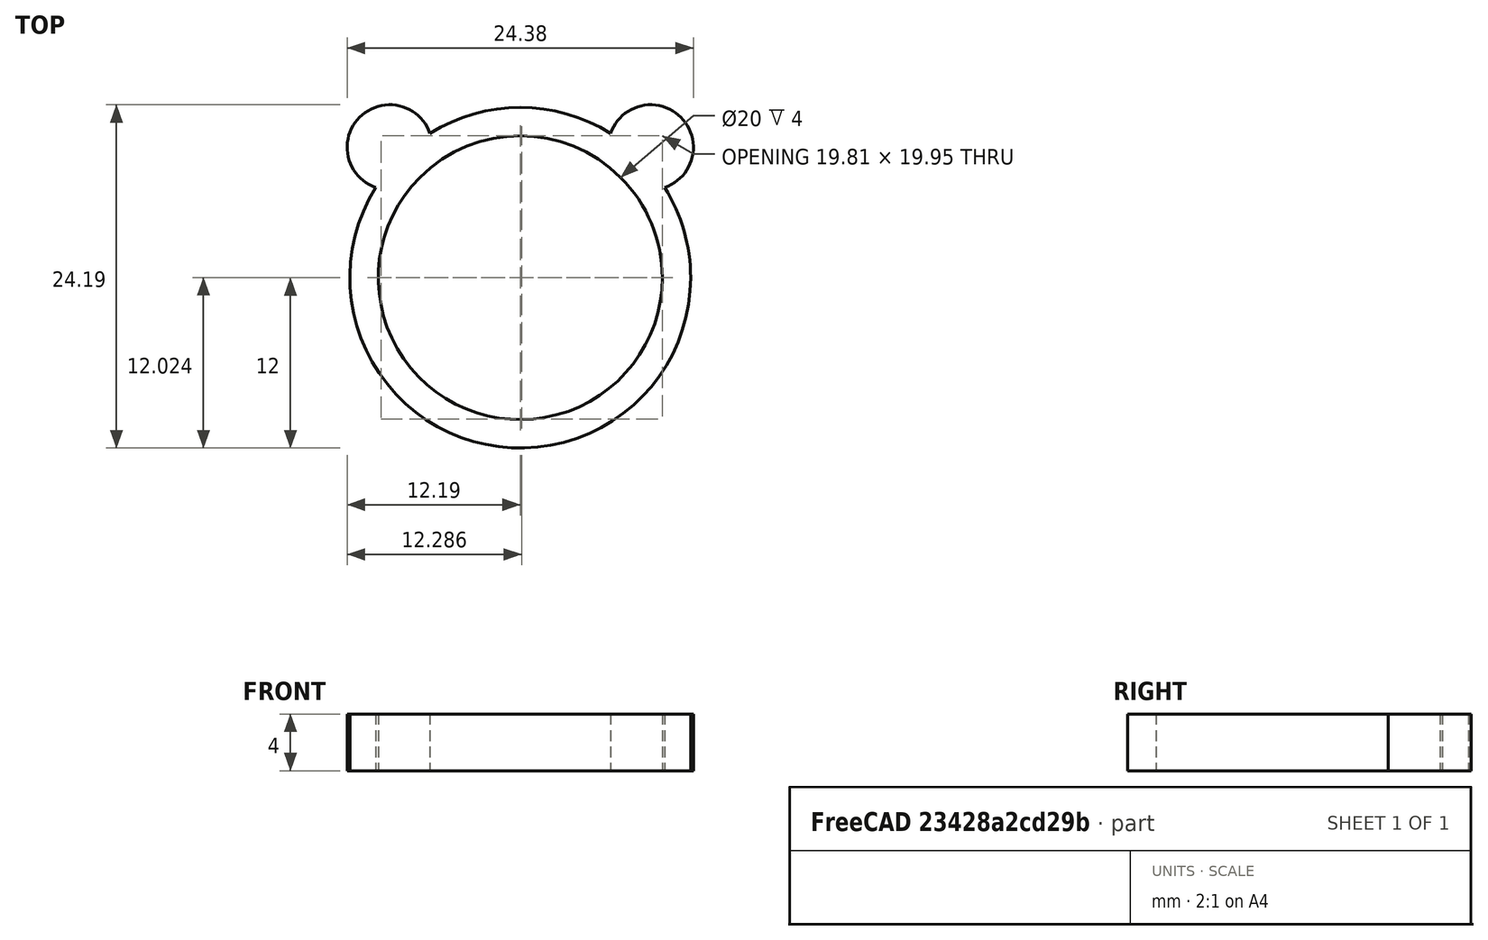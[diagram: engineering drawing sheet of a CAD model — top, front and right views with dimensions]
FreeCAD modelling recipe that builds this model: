
FCSTD DOCUMENT  (FreeCAD 0.17R12412 (Git))
Label: 04-ring-parametric
License: All rights reserved
LicenseURL: http://en.wikipedia.org/wiki/All_rights_reserved
objects: TechDraw::DrawViewDimension×4, Sketcher::SketchObject×2, PartDesign::Pad×2, TechDraw::DrawProjGroupItem×2, TechDraw::DrawHatch×2, PartDesign::Mirrored×1, PartDesign::Body×1, Spreadsheet::Sheet×1, TechDraw::DrawSVGTemplate×1, TechDraw::DrawProjGroup×1, TechDraw::DrawPage×1
note: 8 computed .brp shape members not serialized (recipe doc carries the construction recipe); baked Part::Feature solids carry a one-line shape summary decoded from their .brp

FEATURE [Sketcher::SketchObject] Sketch
  MapMode = 5
  Support = -> [XY_Plane]
  expr: Constraints[1] = param.R + 2
  expr: Constraints[3] = param.R
  sketch-geometry (2):
    g0: Circle CenterX=0 CenterY=0 CenterZ=0 NormalX=0 NormalY=0 NormalZ=1 AngleXU=0 Radius=12
    g1: Circle CenterX=0 CenterY=0 CenterZ=0 NormalX=0 NormalY=0 NormalZ=1 AngleXU=0 Radius=10
  constraints (4):
    c: Coincident(g0,g-1)
    c: Radius(g0) = 12
    c: Coincident(g1,g-1)
    c: Radius(g1) = 10
FEATURE [PartDesign::Pad] Pad
  Length = 4
  Length2 = 100
  Profile = -> Sketch
  Type = 0
  expr: Length = param.H
FEATURE [Sketcher::SketchObject] Sketch001
  ExternalGeometry = -> [Pad]
  MapMode = 5
  Support = -> [XY_Plane]
  expr: Constraints[4] = param.R + 3
  sketch-geometry (2):
    g0: Circle CenterX=-9.19239 CenterY=9.19239 CenterZ=0 NormalX=0 NormalY=0 NormalZ=1 AngleXU=0 Radius=3
    g1: LineSegment [constr] StartX=-9.19239 StartY=9.19239 StartZ=0 EndX=0 EndY=0 EndZ=0
  constraints (5):
    c: Radius(g0) = 3
    c: Coincident(g1,g0)
    c: Coincident(g1,g-1)
    c: Angle(g-2,g1) = 0.785398
    c: Distance(g1) = 13
FEATURE [PartDesign::Pad] Pad001
  BaseFeature = -> Pad
  Length = 3
  Length2 = 100
  Profile = -> Sketch001
  Type = 3
  UpToFace = -> Pad [Face4]
FEATURE [PartDesign::Mirrored] Mirrored
  MirrorPlane = -> YZ_Plane
  Originals = -> [Pad001]
FEATURE [PartDesign::Body] Body
  Group = -> [Sketch,Pad,Sketch001,Pad001,Mirrored]
  Origin = -> Origin
  Tip = -> Mirrored
FEATURE [Spreadsheet::Sheet] Spreadsheet  label="param"
  cells = B2=Radius; C2(R)==20 / 2; B3=height; C3(H)=4
FEATURE [TechDraw::DrawSVGTemplate] Template
  EditableTexts = Designed_by_Name=Designed by Name; Drawing_number=Drawing number; FC-Date=Date; FC-SC=Scale; FC-SH=Sheet; FC-Title=Title; Subtitle=Subtitle; Weight=Weight
  Height = 210
  Orientation = 1
  Width = 297
FEATURE [TechDraw::DrawProjGroupItem] ProjItem  label="Front"
  ArcCenterMarks = true
  CenterScale = 2
  Direction = (0,0,1)
  HardHidden = false
  HiddenWidth = 0.15
  HorizCenterLine = false
  IsoCount = 0
  IsoHidden = false
  IsoVisible = false
  IsoWidth = 0.3
  KeepLabel = false
  LineWidth = 0.7
  Rotation = 0
  RotationVector = (1,0,0)
  Scale = 2
  ScaleType = 0
  SeamHidden = false
  SeamVisible = false
  ShowSectionLine = true
  SmoothHidden = false
  SmoothVisible = false
  Source = -> Body
  Type = 0
  VertCenterLine = false
  X = 0
  Y = 0.000491027
FEATURE [TechDraw::DrawProjGroupItem] ProjItem001  label="Bottom"
  ArcCenterMarks = true
  CenterScale = 2
  Direction = (0,-1,0)
  HardHidden = false
  HiddenWidth = 0.15
  HorizCenterLine = false
  IsoCount = 0
  IsoHidden = false
  IsoVisible = false
  IsoWidth = 0.3
  KeepLabel = false
  LineWidth = 0.7
  Rotation = 0
  RotationVector = (1,0,0)
  Scale = 2
  ScaleType = 0
  SeamHidden = false
  SeamVisible = false
  ShowSectionLine = true
  SmoothHidden = false
  SmoothVisible = false
  Source = -> Body
  Type = 5
  VertCenterLine = false
  X = 0
  Y = 63.3848
FEATURE [TechDraw::DrawProjGroup] ProjGroup
  Anchor = -> ProjItem
  AutoDistribute = true
  CubeDirs = (6) [(0,-1,-6.12323e-17),(0,-6.12323e-17,1),(-1,0,0),(0,6.12323e-17,-1),(1,0,0),(0,1,6.12323e-17)]
  CubeRotations = (6) [(1,0,0),(1,0,0),(0,6.12323e-17,1),(-1,0,0),(0,-6.12323e-17,-1),(1,0,0)]
  KeepLabel = false
  ProjectionType = 0
  Rotation = 0
  Scale = 2
  ScaleType = 0
  Source = -> Body
  Views = -> [ProjItem,ProjItem001]
  X = 66.6272
  Y = 103.516
  spacingX = 15
  spacingY = 15
FEATURE [TechDraw::DrawViewDimension] Dimension
  Font = Sans
  Fontsize = 4
  FormatSpec = %.2f
  KeepLabel = false
  LineWidth = 0.5
  MeasureType = 1
  References2D = -> [ProjItem001]
  Rotation = 0
  Scale = 2
  ScaleType = 0
  Type = 2
  X = 47.4912
  Y = -19.788
FEATURE [TechDraw::DrawViewDimension] Dimension001
  Font = Sans
  Fontsize = 4
  FormatSpec = %.2f
  KeepLabel = false
  LineWidth = 0.5
  MeasureType = 1
  References2D = -> [ProjItem]
  Rotation = 0
  Scale = 2
  ScaleType = 0
  Type = 5
  X = 60.106
  Y = 31.4134
FEATURE [TechDraw::DrawViewDimension] Dimension002
  Font = Sans
  Fontsize = 4
  FormatSpec = %.2f
  KeepLabel = false
  LineWidth = 0.5
  MeasureType = 1
  References2D = -> [ProjItem]
  Rotation = 0
  Scale = 2
  ScaleType = 0
  Type = 1
  X = 77.5241
  Y = -5.83313
FEATURE [TechDraw::DrawViewDimension] Dimension003
  Font = Sans
  Fontsize = 4
  FormatSpec = %.2f
  KeepLabel = false
  LineWidth = 0.5
  MeasureType = 1
  References2D = -> [ProjItem]
  Rotation = 0
  Scale = 2
  ScaleType = 0
  Type = 4
  X = 54.9117
  Y = -36.8551
FEATURE [TechDraw::DrawPage] Page
  KeepUpdated = true
  ProjectionType = 0
  Scale = 2
  Template = -> Template
  Views = -> [ProjGroup,Dimension,Dimension001,Dimension002,Dimension003]
FEATURE [TechDraw::DrawHatch] Hatch  label="HatchF1"
  DirProjection = (0,0,1)
  HatchScale = 1
  Source = -> ProjItem001 [Face1]
FEATURE [TechDraw::DrawHatch] Hatch001  label="Hatch001F1"
  DirProjection = (0,0,1)
  HatchScale = 1
  Source = -> ProjItem001 [Face1]
